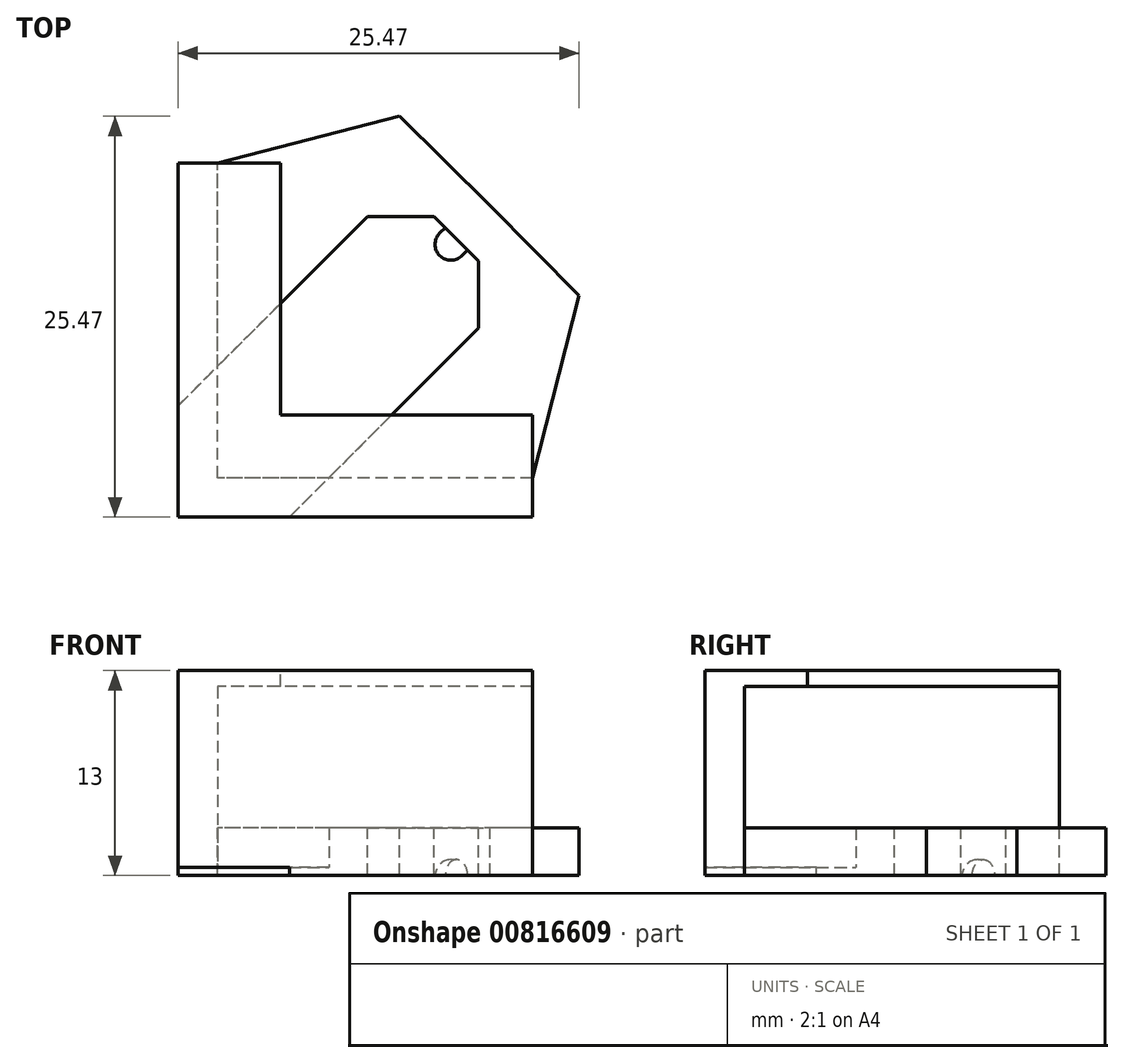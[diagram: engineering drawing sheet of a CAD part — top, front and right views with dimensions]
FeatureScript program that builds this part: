
annotation { "Feature Type Name" : "Feature", "Feature Type Description" : "" }
export const myFeature = defineFeature(function(context is Context, id is Id, definition is map)
    precondition{}
    {
        {
            var Q0;
            Q0=qCreatedBy(makeId("Top.planeOp"),FACE);
            cPlane(context, id + "F0", {"entities" : qUnion([Q0]), "cplaneType" : CPlaneType.OFFSET, "offset" : 4 * mm, "width" : 150 * mm, "height" : 150 * mm});
        }
        {
            var Q0;
            Q0=qCreatedBy(id+"F0.planeOp",FACE);
            var sketch = newSketch(context, id + "F1", { "sketchPlane" : qUnion([Q0])});
            skLineSegment(sketch, "E0", {"start": v(0, 0) * mm, "end": v(0, 20) * mm});
            skLineSegment(sketch, "E1", {"start": v(0, 20) * mm, "end": v(-2.5, 20) * mm});
            skLineSegment(sketch, "E2", {"start": v(-2.5, 20) * mm, "end": v(-2.5, -2.5) * mm});
            skLineSegment(sketch, "E3", {"start": v(-2.5, -2.5) * mm, "end": v(20, -2.5) * mm});
            skLineSegment(sketch, "E4", {"start": v(20, -2.5) * mm, "end": v(20, 0) * mm});
            skLineSegment(sketch, "E5", {"start": v(20, 0) * mm, "end": v(0, 0) * mm});
            skSolve(sketch);
        }
        {
            var Q0;
            Q0 = qSketchRegion(id + "F1", true);
            extrude(context, id + "F2", {"entities" : qUnion([Q0]), "depth" : 6 * mm, "offsetDistance" : 25 * mm});
        }
        {
            var Q0;
            Q0=qCreatedBy(makeId("Top.planeOp"),FACE);
            var sketch = newSketch(context, id + "F3", { "sketchPlane" : qUnion([Q0])});
            skLineSegment(sketch, "E6", {"start": v(-2.5, -2.5) * mm, "end": v(20, 20) * mm, "construction": true});
            skLineSegment(sketch, "E7", {"start": v(-2.5, 20) * mm, "end": v(20, -2.5) * mm, "construction": true});
            skLineSegment(sketch, "E8.top", {"start": v(16.6, 9.52) * mm, "end": v(4.57, -2.5) * mm});
            skLineSegment(sketch, "E8.left", {"start": v(15.18, 15.18) * mm, "end": v(16.6, 13.76) * mm});
            skPoint(sketch, "E8.middle", {"position": v(8.75, 8.75) * mm});
            skLineSegment(sketch, "E9.bottom", {"start": v(22.97, 11.56) * mm, "end": v(17.3, 17.3) * mm});
            skLineSegment(sketch, "E9.left", {"start": v(22.97, 11.56) * mm, "end": v(8.75, -2.5) * mm});
            skLineSegment(sketch, "E10", {"start": v(15.18, 15.18) * mm, "end": v(17.3, 17.3) * mm});
            skLineSegment(sketch, "E11", {"start": v(4.57, -2.5) * mm, "end": v(8.75, -2.5) * mm});
            skLineSegment(sketch, "E12", {"start": v(16.6, 9.52) * mm, "end": v(16.6, 13.76) * mm});
            skPoint(sketch, "E13.orphan", {"position": v(18.71, 11.64) * mm});
            skPoint(sketch, "E14.orphan", {"position": v(11.64, 18.71) * mm});
            skPoint(sketch, "E15.end.orphan", {"position": v(-2.5, 4.57) * mm});
            skLineSegment(sketch, "E16.MirrorCS", {"start": v(-2.5, 4.57) * mm, "end": v(-2.5, 8.75) * mm});
            skLineSegment(sketch, "E17.MirrorCS", {"start": v(9.52, 16.6) * mm, "end": v(-2.5, 4.57) * mm});
            skLineSegment(sketch, "E18.MirrorCS", {"start": v(15.18, 15.18) * mm, "end": v(13.76, 16.6) * mm});
            skLineSegment(sketch, "E19.MirrorCS", {"start": v(9.52, 16.6) * mm, "end": v(13.76, 16.6) * mm});
            skLineSegment(sketch, "E20.MirrorCS", {"start": v(11.56, 22.97) * mm, "end": v(-2.5, 8.75) * mm});
            skLineSegment(sketch, "E21.MirrorCS", {"start": v(11.56, 22.97) * mm, "end": v(17.3, 17.3) * mm});
            skLineSegment(sketch, "E22", {"start": v(22.97, 11.56) * mm, "end": v(20, 0) * mm});
            skLineSegment(sketch, "E23", {"start": v(20, 0) * mm, "end": v(20, -2.5) * mm});
            skLineSegment(sketch, "E24", {"start": v(8.75, -2.5) * mm, "end": v(20, -2.5) * mm});
            skLineSegment(sketch, "E25", {"start": v(11.56, 22.97) * mm, "end": v(0, 20) * mm});
            skLineSegment(sketch, "E26", {"start": v(0, 20) * mm, "end": v(-2.5, 20) * mm});
            skLineSegment(sketch, "E27", {"start": v(-2.5, 20) * mm, "end": v(-2.5, 8.75) * mm});
            skSolve(sketch);
        }
        {
            var Q0;
            Q0 = qSketchRegion(id + "F3", true);
            extrude(context, id + "F4", {"entities" : qUnion([Q0]), "operationType" : NewBodyOperationType.ADD, "depth" : -3 * mm, "offsetDistance" : 25 * mm});
        }
        {
            var Q0;
            Q0 = qSketchRegion(id + "F1", true);
            extrude(context, id + "F5", {"entities" : qUnion([Q0]), "operationType" : NewBodyOperationType.ADD, "depth" : -6.5 * mm, "offsetDistance" : 25 * mm});
        }
        {
            var Q0;
            Q0=makeQuery(id+"F4.opExtrude","SWEPT_FACE",FACE,{"disambiguationData":[OSD([sQuery(id+"F3.wireOp",EDGE,"E8.left"),sQuery(id+"F3.wireOp",EDGE,"E18.MirrorCS")])]});
            var sketch = newSketch(context, id + "F6", { "sketchPlane" : qUnion([Q0])});
            skArc(sketch, "E28", {"start": v(1, -3) * mm, "mid": v(0, -2) * mm, "end": v(-1, -3) * mm});
            skLineSegment(sketch, "E29", {"start": v(-1, -3) * mm, "end": v(1, -3) * mm});
            skSolve(sketch);
        }
        {
            var Q0;
            Q0=makeQuery(id+"F6.imprint","IMPRINT",FACE,{"disambiguationData":[TD([[makeQuery(id+"F6.imprint","IMPRINT",EDGE,{"derivedFrom":sQuery(id+"F6.wireOp",EDGE,"E28")}),1.0]])]});
            extrude(context, id + "F7", {"entities" : qUnion([Q0]), "operationType" : NewBodyOperationType.ADD, "depth" : 1.5 * mm, "offsetDistance" : 25 * mm});
        }
        {
            var Q0;
            Q0=makeQuery(id+"F7.opExtrude","CAP_EDGE",EDGE,{"disambiguationData":[OSD([sQuery(id+"F6.wireOp",EDGE,"E28")])],"isStart":false});
            fillet(context, id + "F8", {"entities" : qUnion([Q0]), "radius" : 1 * mm, "tangentPropagation" : true, "allowEdgeOverflow" : false});
        }
        {
            var Q0;
            Q0=makeQuery(id+"F2.opExtrude","CAP_FACE",FACE,{"disambiguationData":[OSD([sQuery(id+"F1.wireOp",EDGE,"E0"),sQuery(id+"F1.wireOp",EDGE,"E1"),sQuery(id+"F1.wireOp",EDGE,"E2"),sQuery(id+"F1.wireOp",EDGE,"E3"),sQuery(id+"F1.wireOp",EDGE,"E4"),sQuery(id+"F1.wireOp",EDGE,"E5")])],"isStart":false});
            var sketch = newSketch(context, id + "F9", { "sketchPlane" : qUnion([Q0])});
            skLineSegment(sketch, "E30.0", {"start": v(-2.5, 20) * mm, "end": v(-2.5, -2.5) * mm});
            skLineSegment(sketch, "E30.2", {"start": v(20, 4) * mm, "end": v(4, 4) * mm});
            skLineSegment(sketch, "E30.3", {"start": v(-2.5, -2.5) * mm, "end": v(20, -2.5) * mm});
            skLineSegment(sketch, "E30.4", {"start": v(4, 4) * mm, "end": v(4, 20) * mm});
            skLineSegment(sketch, "E31", {"start": v(-2.5, 20) * mm, "end": v(4, 20) * mm});
            skLineSegment(sketch, "E32", {"start": v(20, -2.5) * mm, "end": v(20, 4) * mm});
            skSolve(sketch);
        }
        {
            var Q0;
            Q0 = qSketchRegion(id + "F9", true);
            extrude(context, id + "F10", {"entities" : qUnion([Q0]), "operationType" : NewBodyOperationType.ADD, "depth" : -1 * mm, "offsetDistance" : 25 * mm});
        }
    });
